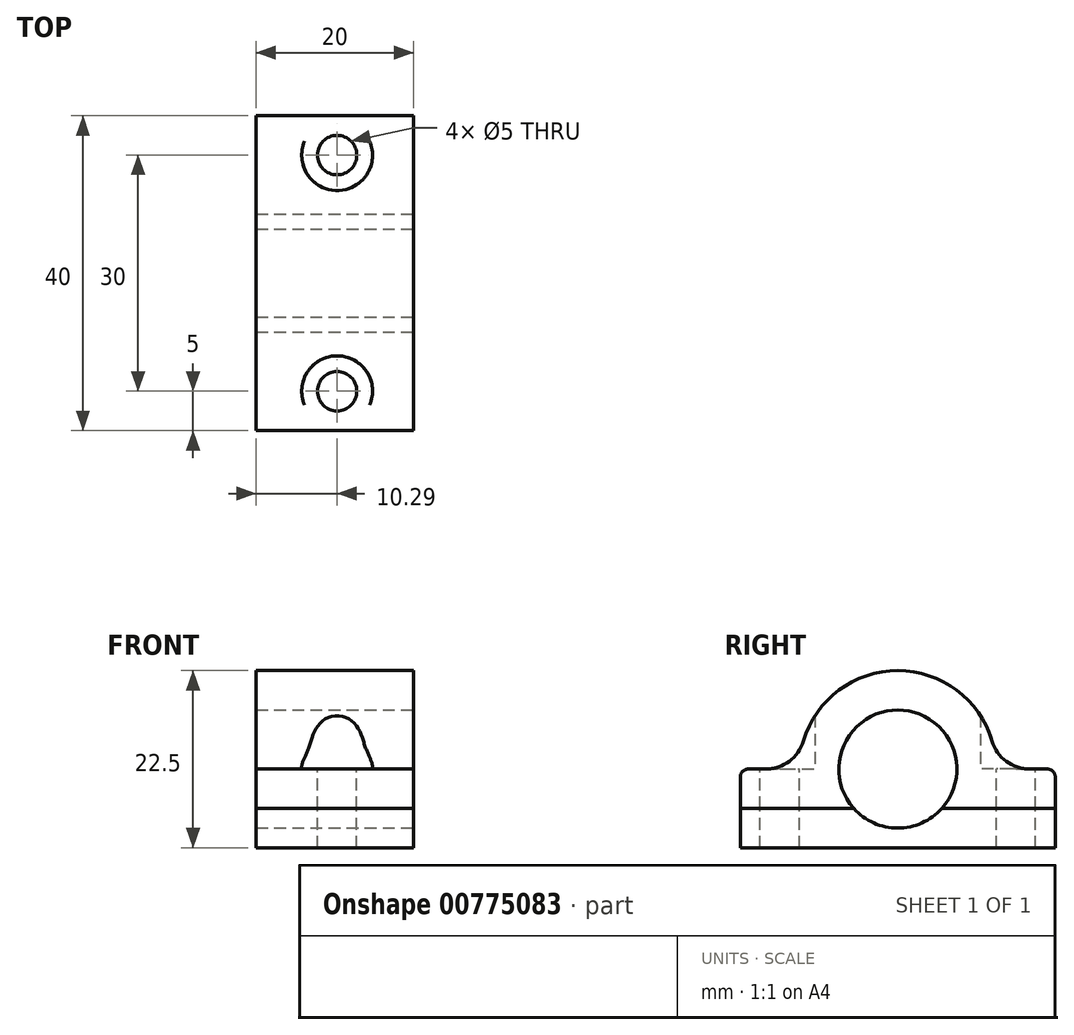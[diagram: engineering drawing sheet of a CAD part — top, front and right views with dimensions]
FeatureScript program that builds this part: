
annotation { "Feature Type Name" : "Feature", "Feature Type Description" : "" }
export const myFeature = defineFeature(function(context is Context, id is Id, definition is map)
    precondition{}
    {
        {
            var Q0;
            Q0=qCreatedBy(makeId("Top.planeOp"),FACE);
            var sketch = newSketch(context, id + "F0", { "sketchPlane" : qUnion([Q0])});
            skLineSegment(sketch, "E0.bottom", {"start": v(-10.3, 20) * mm, "end": v(9.7, 20) * mm});
            skLineSegment(sketch, "E0.top", {"start": v(-10.3, -20) * mm, "end": v(9.7, -20) * mm});
            skLineSegment(sketch, "E0.left", {"start": v(-10.3, 20) * mm, "end": v(-10.3, -20) * mm});
            skLineSegment(sketch, "E0.right", {"start": v(9.7, 20) * mm, "end": v(9.7, -20) * mm});
            skSolve(sketch);
        }
        {
            var Q0;
            Q0 = qSketchRegion(id + "F0", true);
            extrude(context, id + "F1", {"entities" : qUnion([Q0]), "depth" : 5 * mm, "offsetDistance" : 25 * mm});
        }
        {
            var Q0;
            Q0=makeQuery(id+"F1.opExtrude","SWEPT_FACE",FACE,{"disambiguationData":[OSD([sQuery(id+"F0.wireOp",EDGE,"E0.right")])]});
            var sketch = newSketch(context, id + "F2", { "sketchPlane" : qUnion([Q0])});
            skPoint(sketch, "E1.centerSnap0", {"position": v(0, 5) * mm});
            skLineSegment(sketch, "E2", {"start": v(-20, 5) * mm, "end": v(-20, 10) * mm});
            skLineSegment(sketch, "E3", {"start": v(-20, 10) * mm, "end": v(-12.5, 10) * mm});
            skLineSegment(sketch, "E4", {"start": v(20, 10) * mm, "end": v(20, 5) * mm});
            skLineSegment(sketch, "E5.trimOffspring", {"start": v(12.5, 10) * mm, "end": v(20, 10) * mm});
            skLineSegment(sketch, "E6", {"start": v(-20, 5) * mm, "end": v(20, 5) * mm});
            skArc(sketch, "E7.trimOffspring", {"start": v(12.5, 10) * mm, "mid": v(0, 22.5) * mm, "end": v(-12.5, 10) * mm});
            skSolve(sketch);
        }
        {
            var Q0;
            Q0 = qSketchRegion(id + "F2", true);
            var Q1;
            Q1=makeQuery(id+"F1.opExtrude","SWEPT_FACE",FACE,{"disambiguationData":[OSD([sQuery(id+"F0.wireOp",EDGE,"E0.left")])]});
            extrude(context, id + "F3", {"entities" : qUnion([Q0]), "endBound" : BoundingType.UP_TO_SURFACE, "oppositeDirection" : true, "depth" : 25 * mm, "endBoundEntityFace" : qUnion([Q1]), "offsetDistance" : 25 * mm});
        }
        {
            var Q0;
            Q0=makeQuery(id+"F3.opExtrude","CAP_FACE",FACE,{"disambiguationData":[OSD([sQuery(id+"F2.wireOp",EDGE,"E2"),sQuery(id+"F2.wireOp",EDGE,"E3"),sQuery(id+"F2.wireOp",EDGE,"E4"),sQuery(id+"F2.wireOp",EDGE,"E5.trimOffspring"),sQuery(id+"F2.wireOp",EDGE,"E6"),sQuery(id+"F2.wireOp",EDGE,"E7.trimOffspring")])],"isStart":true});
            var sketch = newSketch(context, id + "F4", { "sketchPlane" : qUnion([Q0])});
            skCircle(sketch, "E8", {"center": v(0, 10) * mm, "radius": 7.5 * mm});
            skSolve(sketch);
        }
        {
            var Q0;
            Q0 = qSketchRegion(id + "F4", true);
            var Q1;
            Q1=makeQuery(id+"F3.opExtrude","CAP_FACE",FACE,{"disambiguationData":[OSD([sQuery(id+"F2.wireOp",EDGE,"E2"),sQuery(id+"F2.wireOp",EDGE,"E3"),sQuery(id+"F2.wireOp",EDGE,"E4"),sQuery(id+"F2.wireOp",EDGE,"E5.trimOffspring"),sQuery(id+"F2.wireOp",EDGE,"E6"),sQuery(id+"F2.wireOp",EDGE,"E7.trimOffspring")])],"isStart":false});
            extrude(context, id + "F5", {"entities" : qUnion([Q0]), "operationType" : NewBodyOperationType.REMOVE, "endBound" : BoundingType.UP_TO_SURFACE, "oppositeDirection" : true, "depth" : 25 * mm, "endBoundEntityFace" : qUnion([Q1]), "offsetDistance" : 25 * mm});
        }
        {
            var Q0;
            Q0=makeQuery(id+"F3.opExtrude","SWEPT_EDGE",EDGE,{"disambiguationData":[OSD([sQuery(id+"F2.wireOp",EDGE,"E5.trimOffspring"),sQuery(id+"F2.wireOp",EDGE,"E7.trimOffspring")])]});
            var Q1;
            Q1=makeQuery(id+"F3.opExtrude","SWEPT_EDGE",EDGE,{"disambiguationData":[OSD([sQuery(id+"F2.wireOp",EDGE,"E3"),sQuery(id+"F2.wireOp",EDGE,"E7.trimOffspring")])]});
            fillet(context, id + "F6", {"entities" : qUnion([Q0, Q1]), "radius" : 5 * mm, "tangentPropagation" : true, "allowEdgeOverflow" : false});
        }
        {
            var Q0;
            Q0=makeQuery(id+"F3.opExtrude","SWEPT_FACE",FACE,{"disambiguationData":[OSD([sQuery(id+"F2.wireOp",EDGE,"E3")])]});
            var sketch = newSketch(context, id + "F7", { "sketchPlane" : qUnion([Q0])});
            skCircle(sketch, "E9", {"center": v(0, 15) * mm, "radius": 2.5 * mm});
            skCircle(sketch, "E10", {"center": v(0, -15) * mm, "radius": 2.5 * mm});
            skSolve(sketch);
        }
        {
            var Q0;
            Q0 = qSketchRegion(id + "F7", true);
            extrude(context, id + "F8", {"entities" : qUnion([Q0]), "operationType" : NewBodyOperationType.REMOVE, "endBound" : BoundingType.SYMMETRIC, "oppositeDirection" : true, "depth" : 25 * mm, "offsetDistance" : 25 * mm});
        }
        {
            var Q0;
            Q0=makeQuery(id+"F3.opExtrude","SWEPT_FACE",FACE,{"disambiguationData":[OSD([sQuery(id+"F2.wireOp",EDGE,"E3")])]});
            var sketch = newSketch(context, id + "F9", { "sketchPlane" : qUnion([Q0])});
            skCircle(sketch, "E11", {"center": v(0, -15) * mm, "radius": 4.5 * mm});
            skCircle(sketch, "E12", {"center": v(0, 15) * mm, "radius": 4.5 * mm});
            skSolve(sketch);
        }
        {
            var Q0;
            Q0 = qSketchRegion(id + "F9", true);
            extrude(context, id + "F10", {"entities" : qUnion([Q0]), "operationType" : NewBodyOperationType.REMOVE, "depth" : 8 * mm, "offsetDistance" : 25 * mm});
        }
        {
            var Q0;
            Q0=makeQuery(id+"F3.opExtrude","SWEPT_EDGE",EDGE,{"disambiguationData":[OSD([sQuery(id+"F2.wireOp",EDGE,"E4"),sQuery(id+"F2.wireOp",EDGE,"E5.trimOffspring")])]});
            var Q1;
            Q1=makeQuery(id+"F3.opExtrude","SWEPT_EDGE",EDGE,{"disambiguationData":[OSD([sQuery(id+"F2.wireOp",EDGE,"E2"),sQuery(id+"F2.wireOp",EDGE,"E3")])]});
            fillet(context, id + "F11", {"entities" : qUnion([Q0, Q1]), "radius" : 1 * mm, "tangentPropagation" : true, "allowEdgeOverflow" : false});
        }
    });
